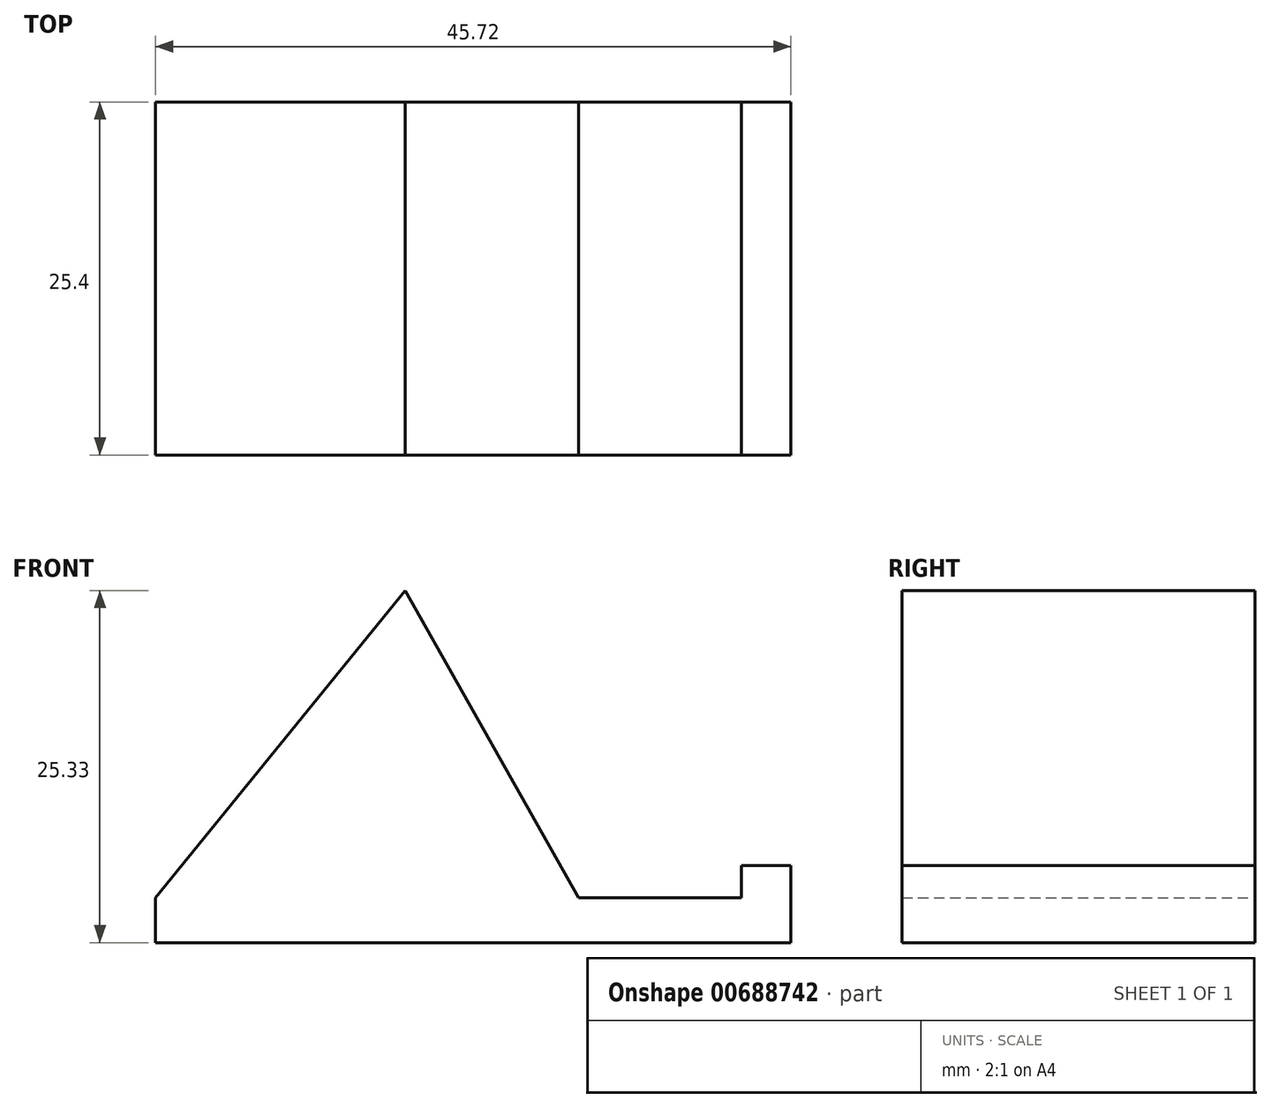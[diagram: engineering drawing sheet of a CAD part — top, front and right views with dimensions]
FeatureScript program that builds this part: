
annotation { "Feature Type Name" : "Feature", "Feature Type Description" : "" }
export const myFeature = defineFeature(function(context is Context, id is Id, definition is map)
    precondition{}
    {
        {
            var Q0;
            Q0=qCreatedBy(makeId("Front.planeOp"),FACE);
            var sketch = newSketch(context, id + "F0", { "sketchPlane" : qUnion([Q0])});
            skLineSegment(sketch, "E0", {"start": v(0, 0) * mm, "end": v(-45.72, 0) * mm});
            skLineSegment(sketch, "E1", {"start": v(-45.72, 0) * mm, "end": v(-45.72, 3.21) * mm});
            skLineSegment(sketch, "E2", {"start": v(-45.72, 3.21) * mm, "end": v(0, 3.21) * mm});
            skLineSegment(sketch, "E3", {"start": v(0, 3.21) * mm, "end": v(0, 0) * mm});
            skLineSegment(sketch, "E4", {"start": v(0, 3.21) * mm, "end": v(0, 5.54) * mm});
            skLineSegment(sketch, "E5", {"start": v(0, 5.54) * mm, "end": v(-3.56, 5.54) * mm});
            skLineSegment(sketch, "E6", {"start": v(-3.56, 5.54) * mm, "end": v(-3.56, 3.21) * mm});
            skLineSegment(sketch, "E7", {"start": v(-15.28, 3.21) * mm, "end": v(-27.77, 25.33) * mm});
            skLineSegment(sketch, "E8", {"start": v(-45.72, 3.21) * mm, "end": v(-27.77, 25.33) * mm});
            skSolve(sketch);
        }
        {
            var Q0;
            Q0 = qSketchRegion(id + "F0", true);
            extrude(context, id + "F1", {"entities" : qUnion([Q0]), "depth" : 25.4 * mm, "offsetDistance" : 25.4 * mm});
        }
    });
